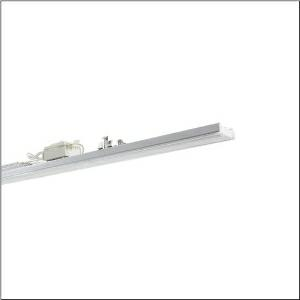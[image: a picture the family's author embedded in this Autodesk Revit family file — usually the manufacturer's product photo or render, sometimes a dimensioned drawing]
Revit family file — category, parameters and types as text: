
# Revit family: licross_21_recessed_mo_52te11cn49xg
name_source: partatom
category: Lighting Fixtures
units: mm (PartAtom-declared; Revit-internal decimal feet)

## family parameters
Cut with Voids When Loaded = No
Host = Face
Light Source = No
Part Type = Normal
Room Calculation Point = No
Round Connector Dimension = Use Diameter
Shared = No

## types (1)
- --- (1 x LED, 9120 lm, 49.9 W, 4000K)
    Apparent Load = 50 VA
    CIE Flux Codes = 89 96 99 100 100
    Color Rendering = 80
    Color Temperature = 4000K
    Default Elevation = 1800 mm
    Description = Licross 21 Recessed MO, luminaire insert, of sheet steel, galvanised, coil coated, white, length: 1.500mm, width: 66mm, height: 67mm, LED rated luminous flux: 9.120lm, light colour: 840, SDCM (Standard Deviation of Colour Matching)MacAdam ≤ 3 SDCM (initial), control gear: ON/OFF Multilumen, CLOi, with plug, 3-pole, with phase selection, mains connection: 220..240V, AC, 50/60Hz, start of lifetime: 50W, end of service life: 61W, internal wiring halogen-free, primary light control with lens, of plastic, primary optical cover: cover, of PMMA, light emission: direct distribution, primary light characteristic: symmetric, protection rating (complete): IP54, insulation class (complete): insulation class I (protective earthing), certification: CE, ENEC, VDE, UKCA, protection symbol: D if used in an environment with non-conductive dust loads with corresponding accessories, impact resistance: IK06, permissible ambient temperature for indoor applications: -35..+40°C, corresponds to IFS (International Featured Standards) requirements for safety and quality in the food industry, reducing of maximum allowable ambient temperature of 5°C with ceiling mounting, LABS conformity tested according to VDMA 24364:2018-05, The light source and the operating device comply with the requirements of the Ecodesign Regulation (EU) 2019/2020 and are replaceable in accordance with this regulation, packaging unit: 1 piece
    Height = 58 mm
    Lamp = 1 x LED
    Lamp Light Flux = 9120 lm
    Lamp Power = 49.9 W
    Lamp count = 1
    Length = 1500 mm
    Luminous efficacy = 183 lm/W
    Manufacturer = Siteco
    ModVariant = No
    Model = 52TE11CN49XG
    Mounting Place = Ceiling
    Mounting Type = Pendant
    Number of Poles = 1
    OnlyDefault = Yes
    Power Factor = 1
    Product Name = Licross 21 Recessed MO
    Product group = luminaire insert | ceiling pendant
    ProductGroupID = 901
    Protection Class = Protection class I
    Protection Degree = IP 54
    RLX_Detail_Level = 1
    RLX_Emergency_Light_Flux = 0 lm
    RLX_Emergency_Type = 0
    RLX_Emergency_Type_DB = No
    RlxData = <blob elided: 22537 chars, md5=bd5c8c03>
    Socket = socket
    Standby Power = 0 W
    System Light Flux = 9120 lm
    System Power = 50 W
    Type Comments = factory setting: luminous flux: 100 % | (A | C | E) | 116 mA
    Type Image = l_1296930.jpg
    URL = http://relux.com
    VarID = @adj_110617
    Voltage = 0 V
    Weight = 0.00 kg
    Width = 66 mm

## geometry (parser evidence)
native form markers: Blend x4, Sweep x12
no freeform markers — native parametric forms only
